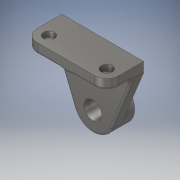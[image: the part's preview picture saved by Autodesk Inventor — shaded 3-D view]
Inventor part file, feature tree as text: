
AUTODESK INVENTOR PART (.ipt)
format: ipt  version: 2019 (Build 230136000, 136)  size: 325,120 bytes
history: native  units: mm
features: extrude x5, sketch x4, fillet x2, plane x1, rib x1
ambient origin geometry x8: Origin, YZ Plane, XZ Plane, XY Plane, X Axis, Y Axis, Z Axis, Center Point
bodies: Solid1 (feature_tree)
feature tree (13):
  extrude  "Extrusion1"  Depth=41.0mm
  sketch  "Sketch2"  dims[d2=18.0mm d3=22.0mm d4=0.0mm]
  extrude  "Extrusion2"  Depth=22.0mm TaperAngle=0.0deg
  extrude  "Extrusion3"  Depth=41.0mm
  plane  "Work Plane1"
  rib  "Rib1"
  sketch  "Sketch6"  dims[d7=10.0mm d8=10.0mm d9=0.0mm d10=27.0mm d11=0.0mm d12=-41.0mm d17=1.0mm d18=10.0mm d19=0.0mm d20=0.0mm d21=1.0mm d22=1.0mm d23=11.0mm d24=22.0mm d25=22.0mm d26=11.0mm d27=12.0mm d28=12.0mm d29=12.0mm d30=12.0mm d31=27.0mm d32=0.0mm d33=4.0mm d34=0.0mm d35=12.0mm d37=2.0mm]
  extrude  "Extrusion4"  Depth=10.0mm TaperAngle=0.0deg
  extrude  "Extrusion5"  Depth=27.0mm TaperAngle=0.0deg
  fillet  "Fillet1"  [1 undecoded]
  fillet  "Fillet3"  Radius=1.0mm
  sketch  "Sketch1"  dims[d0=40.0mm d1=41.0mm]
  sketch  "Sketch5"  dims[d5=82.0mm d6=41.0mm]
note: 1 required parameter value undecoded (feature->parameter linkage not recoverable at this tier; creation-order binding heuristic only, values carry confidence <= 0.55)
